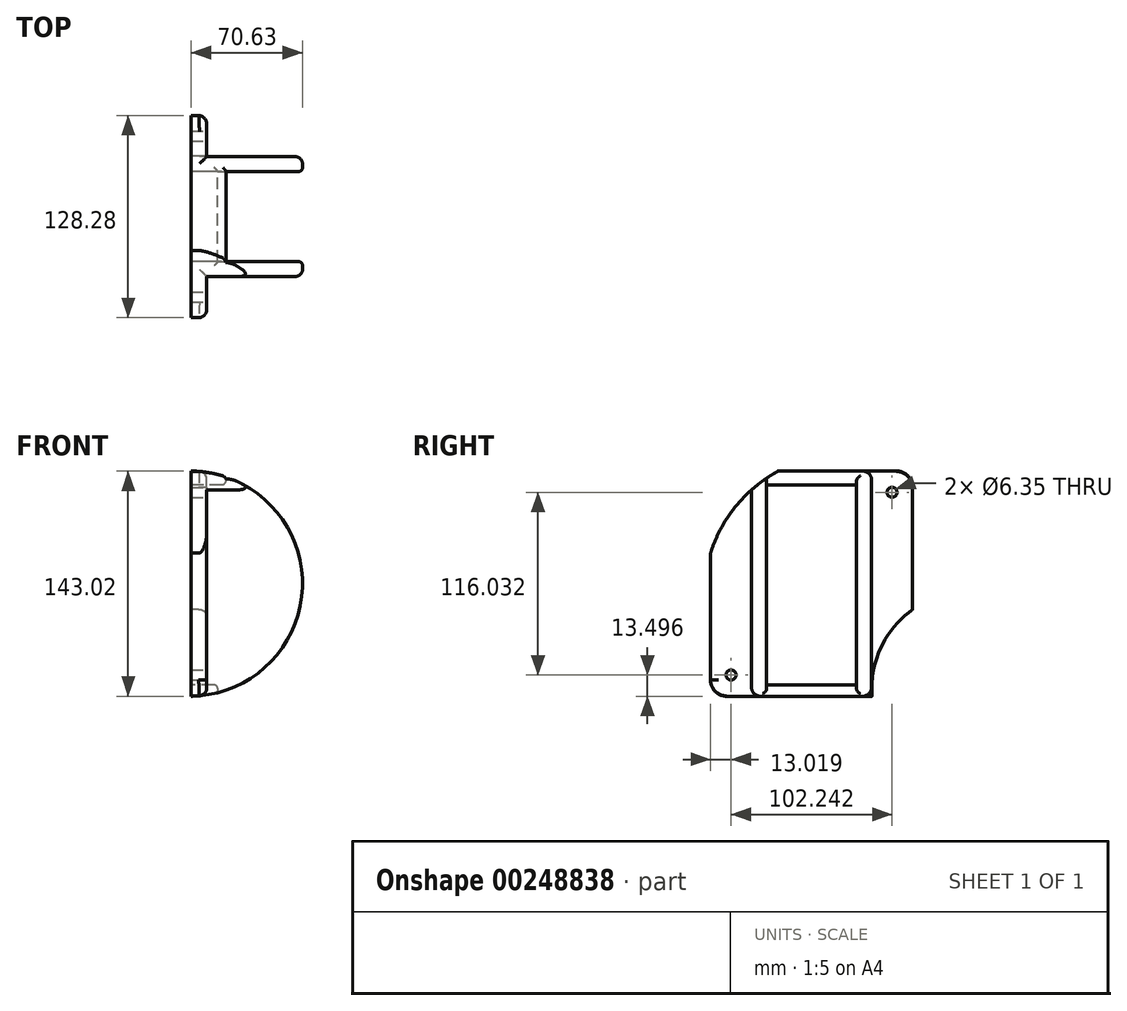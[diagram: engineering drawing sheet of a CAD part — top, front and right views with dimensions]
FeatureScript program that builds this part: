
annotation { "Feature Type Name" : "Feature", "Feature Type Description" : "" }
export const myFeature = defineFeature(function(context is Context, id is Id, definition is map)
    precondition{}
    {
        {
            var Q0;
            Q0=qCreatedBy(makeId("Front.planeOp"),FACE);
            var sketch = newSketch(context, id + "F0", { "sketchPlane" : qUnion([Q0])});
            skArc(sketch, "E0", {"start": v(0, -70.82) * mm, "mid": v(70.63, 0.7) * mm, "end": v(0, 72.2) * mm});
            skLineSegment(sketch, "E1", {"start": v(0, 72.2) * mm, "end": v(0, -70.82) * mm});
            skLineSegment(sketch, "E2", {"start": v(9.79, 71.4) * mm, "end": v(9.79, -70.02) * mm});
            skSolve(sketch);
        }
        {
            var Q0;
            Q0 = qSketchRegion(id + "F0", true);
            extrude(context, id + "F1", {"entities" : qUnion([Q0]), "endBound" : BoundingType.SYMMETRIC, "depth" : 76.2 * mm});
        }
        {
            var Q0;
            Q0 = qSketchRegion(id + "F0", true);
            extrude(context, id + "F2", {"entities" : qUnion([Q0]), "operationType" : NewBodyOperationType.ADD, "depth" : 25.4 * mm});
        }
        {
            var Q0;
            {var subQ0=sQuery(id+"F0.wireOp",EDGE,"E1");Q0=makeQuery(id+"F0.imprint","IMPRINT",FACE,{"disambiguationData":[TD([[makeQuery(id+"F0.imprint","IMPRINT",EDGE,{"derivedFrom":subQ0}),1.0]])]});}
            extrude(context, id + "F3", {"entities" : qUnion([Q0]), "operationType" : NewBodyOperationType.ADD, "endBound" : BoundingType.SYMMETRIC, "depth" : 128.28 * mm});
        }
        {
            var Q0;
            {var subQ0=sQuery(id+"F0.wireOp",EDGE,"E1");Q0=makeQuery(id+"F3.boolean.opBoolean","MERGE",FACE,{"derivedFrom":[makeQuery(id+"F1.opExtrude","SWEPT_FACE",FACE,{"disambiguationData":[OSD([subQ0])]}),makeQuery(id+"F3.opExtrude","SWEPT_FACE",FACE,{"disambiguationData":[OSD([subQ0])]})]});}
            var sketch = newSketch(context, id + "F4", { "sketchPlane" : qUnion([Q0])});
            skLineSegment(sketch, "E3.bottom", {"start": v(28.58, -63.5) * mm, "end": v(-28.58, -63.5) * mm});
            skLineSegment(sketch, "E3.top", {"start": v(28.58, 63.5) * mm, "end": v(-28.57, 63.5) * mm});
            skLineSegment(sketch, "E3.left", {"start": v(28.58, -63.5) * mm, "end": v(28.58, 63.5) * mm});
            skLineSegment(sketch, "E3.right", {"start": v(-28.58, -63.5) * mm, "end": v(-28.57, 63.5) * mm});
            skPoint(sketch, "E3.middle", {"position": v(0, 0) * mm});
            skSolve(sketch);
        }
        {
            var Q0;
            Q0 = qSketchRegion(id + "F4", true);
            extrude(context, id + "F5", {"entities" : qUnion([Q0]), "operationType" : NewBodyOperationType.REMOVE, "oppositeDirection" : true, "depth" : 76.2 * mm});
        }
        {
            var Q0;
            {var subQ0=sQuery(id+"F0.wireOp",EDGE,"E2");var subQ1=sQuery(id+"F0.wireOp",EDGE,"E1");var subQ2=sQuery(id+"F0.wireOp",EDGE,"E0");Q0=makeQuery(id+"F3.boolean.opBoolean","SPLIT",FACE,{"disambiguationData":[TD([makeQuery(id+"F1.opExtrude","CAP_FACE",FACE,{"disambiguationData":[OSD([subQ2,subQ1])],"isStart":true})])],"derivedFrom":makeQuery(id+"F3.opExtrude","SWEPT_FACE",FACE,{"disambiguationData":[OSD([subQ0])]})});}
            var sketch = newSketch(context, id + "F6", { "sketchPlane" : qUnion([Q0])});
            skCircle(sketch, "E4", {"center": v(51.12, 58.7) * mm, "radius": 3.18 * mm});
            skPoint(sketch, "E4.centerSnap0", {"position": v(51.12, 71.4) * mm});
            skSolve(sketch);
        }
        {
            var Q0;
            Q0=makeQuery(id+"F6.imprint","IMPRINT",FACE,{"disambiguationData":[TD([[makeQuery(id+"F6.imprint","IMPRINT",EDGE,{"derivedFrom":sQuery(id+"F6.wireOp",EDGE,"E4")}),-1.0]])]});
            var sketch = newSketch(context, id + "F7", { "sketchPlane" : qUnion([Q0])});
            skCircle(sketch, "E5", {"center": v(51.84, -57.32) * mm, "radius": 3.17 * mm});
            skSolve(sketch);
        }
        {
            var Q0;
            {var subQ0=sQuery(id+"F0.wireOp",EDGE,"E1");var subQ1=sQuery(id+"F0.wireOp",EDGE,"E0");var subQ2=sQuery(id+"F0.wireOp",EDGE,"E2");Q0=makeQuery(id+"F3.boolean.opBoolean","SPLIT",FACE,{"disambiguationData":[TD([makeQuery(id+"F1.opExtrude","CAP_FACE",FACE,{"disambiguationData":[OSD([subQ1,subQ0])],"isStart":false})])],"derivedFrom":makeQuery(id+"F3.opExtrude","SWEPT_FACE",FACE,{"disambiguationData":[OSD([subQ2])]})});}
            var sketch = newSketch(context, id + "F8", { "sketchPlane" : qUnion([Q0])});
            skCircle(sketch, "E6", {"center": v(-51.12, 58.7) * mm, "radius": 3.17 * mm});
            skPoint(sketch, "E6.centerSnap0", {"position": v(-51.12, 71.4) * mm});
            skCircle(sketch, "E7", {"center": v(-51.12, -57.32) * mm, "radius": 3.17 * mm});
            skPoint(sketch, "E7.centerSnap0", {"position": v(-51.12, -70.02) * mm});
            skSolve(sketch);
        }
        {
            var Q0;
            Q0 = qSketchRegion(id + "F8", true);
            extrude(context, id + "F9", {"entities" : qUnion([Q0]), "operationType" : NewBodyOperationType.REMOVE, "oppositeDirection" : true, "depth" : 25.4 * mm});
        }
        {
            var Q0;
            Q0 = qSketchRegion(id + "F7", true);
            extrude(context, id + "F10", {"entities" : qUnion([Q0]), "operationType" : NewBodyOperationType.REMOVE, "oppositeDirection" : true, "depth" : 25.4 * mm});
        }
        {
            var Q0;
            Q0 = qSketchRegion(id + "F6", true);
            extrude(context, id + "F11", {"entities" : qUnion([Q0]), "operationType" : NewBodyOperationType.REMOVE, "oppositeDirection" : true, "depth" : 25.4 * mm});
        }
        {
            var Q0;
            {var subQ0=sQuery(id+"F0.wireOp",EDGE,"E0");Q0=makeQuery(id+"F3.opExtrude","CAP_EDGE",EDGE,{"disambiguationData":[OSD([subQ0]),TDD([makeQuery(id+"F0.imprint","IMPRINT",EDGE,{"disambiguationData":[TD([[makeQuery(id+"F0.imprint","INTERSECT",VERTEX,{"disambiguationData":[OD(1.0)],"derivedFrom":[subQ0,sQuery(id+"F0.wireOp",EDGE,"E1")]}),1.0]])],"derivedFrom":subQ0})])],"isStart":true});}
            var Q1;
            {var subQ0=sQuery(id+"F0.wireOp",EDGE,"E0");Q1=makeQuery(id+"F3.opExtrude","CAP_EDGE",EDGE,{"disambiguationData":[OSD([subQ0]),TDD([makeQuery(id+"F0.imprint","IMPRINT",EDGE,{"disambiguationData":[TD([[makeQuery(id+"F0.imprint","INTERSECT",VERTEX,{"disambiguationData":[OD(0.0)],"derivedFrom":[subQ0,sQuery(id+"F0.wireOp",EDGE,"E1")]}),-1.0]])],"derivedFrom":subQ0})])],"isStart":true});}
            var Q2;
            {var subQ0=sQuery(id+"F0.wireOp",EDGE,"E0");Q2=makeQuery(id+"F3.opExtrude","CAP_EDGE",EDGE,{"disambiguationData":[OSD([subQ0]),TDD([makeQuery(id+"F0.imprint","IMPRINT",EDGE,{"disambiguationData":[TD([[makeQuery(id+"F0.imprint","INTERSECT",VERTEX,{"disambiguationData":[OD(0.0)],"derivedFrom":[subQ0,sQuery(id+"F0.wireOp",EDGE,"E1")]}),-1.0]])],"derivedFrom":subQ0})])],"isStart":false});}
            var Q3;
            {var subQ0=sQuery(id+"F0.wireOp",EDGE,"E0");Q3=makeQuery(id+"F3.opExtrude","CAP_EDGE",EDGE,{"disambiguationData":[OSD([subQ0]),TDD([makeQuery(id+"F0.imprint","IMPRINT",EDGE,{"disambiguationData":[TD([[makeQuery(id+"F0.imprint","INTERSECT",VERTEX,{"disambiguationData":[OD(1.0)],"derivedFrom":[subQ0,sQuery(id+"F0.wireOp",EDGE,"E1")]}),1.0]])],"derivedFrom":subQ0})])],"isStart":false});}
            fillet(context, id + "F12", {"entities" : qUnion([Q0, Q1, Q2, Q3]), "radius" : 10.16 * mm, "tangentPropagation" : true, "allowEdgeOverflow" : false});
        }
        {
            var Q0;
            {var subQ0=sQuery(id+"F0.wireOp",EDGE,"E1");var subQ1=sQuery(id+"F0.wireOp",EDGE,"E0");Q0=makeQuery(id+"F5.boolean.opBoolean","INTERSECT",EDGE,{"derivedFrom":[makeQuery(id+"F3.boolean.opBoolean","MERGE",FACE,{"derivedFrom":[makeQuery(id+"F1.opExtrude","SWEPT_FACE",FACE,{"disambiguationData":[OSD([subQ1])]}),makeQuery(id+"F3.opExtrude","SWEPT_FACE",FACE,{"disambiguationData":[OSD([subQ1]),TDD([makeQuery(id+"F0.imprint","IMPRINT",EDGE,{"disambiguationData":[TD([[makeQuery(id+"F0.imprint","INTERSECT",VERTEX,{"disambiguationData":[OD(0.0)],"derivedFrom":[subQ1,subQ0]}),-1.0]])],"derivedFrom":subQ1})])]}),makeQuery(id+"F3.opExtrude","SWEPT_FACE",FACE,{"disambiguationData":[OSD([subQ1]),TDD([makeQuery(id+"F0.imprint","IMPRINT",EDGE,{"disambiguationData":[TD([[makeQuery(id+"F0.imprint","INTERSECT",VERTEX,{"disambiguationData":[OD(1.0)],"derivedFrom":[subQ1,subQ0]}),1.0]])],"derivedFrom":subQ1})])]})]}),makeQuery(id+"F5.opExtrude","SWEPT_FACE",FACE,{"disambiguationData":[OSD([sQuery(id+"F4.wireOp",EDGE,"E3.bottom")])]})]});}
            var Q1;
            {var subQ0=sQuery(id+"F0.wireOp",EDGE,"E1");var subQ1=sQuery(id+"F0.wireOp",EDGE,"E0");Q1=makeQuery(id+"F5.boolean.opBoolean","INTERSECT",EDGE,{"derivedFrom":[makeQuery(id+"F3.boolean.opBoolean","MERGE",FACE,{"derivedFrom":[makeQuery(id+"F1.opExtrude","SWEPT_FACE",FACE,{"disambiguationData":[OSD([subQ1])]}),makeQuery(id+"F3.opExtrude","SWEPT_FACE",FACE,{"disambiguationData":[OSD([subQ1]),TDD([makeQuery(id+"F0.imprint","IMPRINT",EDGE,{"disambiguationData":[TD([[makeQuery(id+"F0.imprint","INTERSECT",VERTEX,{"disambiguationData":[OD(0.0)],"derivedFrom":[subQ1,subQ0]}),-1.0]])],"derivedFrom":subQ1})])]}),makeQuery(id+"F3.opExtrude","SWEPT_FACE",FACE,{"disambiguationData":[OSD([subQ1]),TDD([makeQuery(id+"F0.imprint","IMPRINT",EDGE,{"disambiguationData":[TD([[makeQuery(id+"F0.imprint","INTERSECT",VERTEX,{"disambiguationData":[OD(1.0)],"derivedFrom":[subQ1,subQ0]}),1.0]])],"derivedFrom":subQ1})])]})]}),makeQuery(id+"F5.opExtrude","SWEPT_FACE",FACE,{"disambiguationData":[OSD([sQuery(id+"F4.wireOp",EDGE,"E3.top")])]})]});}
            fillet(context, id + "F13", {"entities" : qUnion([Q0, Q1]), "radius" : 2.84 * mm, "tangentPropagation" : true, "allowEdgeOverflow" : false});
        }
        {
            var Q0;
            Q0=makeQuery(id+"F1.opExtrude","CAP_EDGE",EDGE,{"disambiguationData":[OSD([sQuery(id+"F0.wireOp",EDGE,"E0")])],"isStart":true});
            var Q1;
            Q1=makeQuery(id+"F1.opExtrude","CAP_EDGE",EDGE,{"disambiguationData":[OSD([sQuery(id+"F0.wireOp",EDGE,"E0")])],"isStart":false});
            fillet(context, id + "F14", {"entities" : qUnion([Q0, Q1]), "radius" : 4.57 * mm, "tangentPropagation" : true, "allowEdgeOverflow" : false});
        }
        {
            var Q0;
            {var subQ0=sQuery(id+"F0.wireOp",EDGE,"E1");var subQ1=sQuery(id+"F0.wireOp",EDGE,"E0");Q0=makeQuery(id+"F5.boolean.opBoolean","INTERSECT",EDGE,{"derivedFrom":[makeQuery(id+"F3.boolean.opBoolean","MERGE",FACE,{"derivedFrom":[makeQuery(id+"F1.opExtrude","SWEPT_FACE",FACE,{"disambiguationData":[OSD([subQ1])]}),makeQuery(id+"F3.opExtrude","SWEPT_FACE",FACE,{"disambiguationData":[OSD([subQ1]),TDD([makeQuery(id+"F0.imprint","IMPRINT",EDGE,{"disambiguationData":[TD([[makeQuery(id+"F0.imprint","INTERSECT",VERTEX,{"disambiguationData":[OD(0.0)],"derivedFrom":[subQ1,subQ0]}),-1.0]])],"derivedFrom":subQ1})])]}),makeQuery(id+"F3.opExtrude","SWEPT_FACE",FACE,{"disambiguationData":[OSD([subQ1]),TDD([makeQuery(id+"F0.imprint","IMPRINT",EDGE,{"disambiguationData":[TD([[makeQuery(id+"F0.imprint","INTERSECT",VERTEX,{"disambiguationData":[OD(1.0)],"derivedFrom":[subQ1,subQ0]}),1.0]])],"derivedFrom":subQ1})])]})]}),makeQuery(id+"F5.opExtrude","SWEPT_FACE",FACE,{"disambiguationData":[OSD([sQuery(id+"F4.wireOp",EDGE,"E3.right")])]})]});}
            var Q1;
            {var subQ0=sQuery(id+"F0.wireOp",EDGE,"E1");var subQ1=sQuery(id+"F0.wireOp",EDGE,"E0");Q1=makeQuery(id+"F5.boolean.opBoolean","INTERSECT",EDGE,{"derivedFrom":[makeQuery(id+"F3.boolean.opBoolean","MERGE",FACE,{"derivedFrom":[makeQuery(id+"F1.opExtrude","SWEPT_FACE",FACE,{"disambiguationData":[OSD([subQ1])]}),makeQuery(id+"F3.opExtrude","SWEPT_FACE",FACE,{"disambiguationData":[OSD([subQ1]),TDD([makeQuery(id+"F0.imprint","IMPRINT",EDGE,{"disambiguationData":[TD([[makeQuery(id+"F0.imprint","INTERSECT",VERTEX,{"disambiguationData":[OD(0.0)],"derivedFrom":[subQ1,subQ0]}),-1.0]])],"derivedFrom":subQ1})])]}),makeQuery(id+"F3.opExtrude","SWEPT_FACE",FACE,{"disambiguationData":[OSD([subQ1]),TDD([makeQuery(id+"F0.imprint","IMPRINT",EDGE,{"disambiguationData":[TD([[makeQuery(id+"F0.imprint","INTERSECT",VERTEX,{"disambiguationData":[OD(1.0)],"derivedFrom":[subQ1,subQ0]}),1.0]])],"derivedFrom":subQ1})])]})]}),makeQuery(id+"F5.opExtrude","SWEPT_FACE",FACE,{"disambiguationData":[OSD([sQuery(id+"F4.wireOp",EDGE,"E3.left")])]})]});}
            fillet(context, id + "F15", {"entities" : qUnion([Q0, Q1]), "radius" : 2.54 * mm, "tangentPropagation" : true, "allowEdgeOverflow" : false});
        }
        {
            var Q0;
            Q0=makeQuery(id+"F3.opExtrude","CAP_EDGE",EDGE,{"disambiguationData":[OSD([sQuery(id+"F0.wireOp",EDGE,"E2")])],"isStart":true});
            var Q1;
            Q1=makeQuery(id+"F3.opExtrude","CAP_EDGE",EDGE,{"disambiguationData":[OSD([sQuery(id+"F0.wireOp",EDGE,"E2")])],"isStart":false});
            fillet(context, id + "F16", {"entities" : qUnion([Q0, Q1]), "radius" : 5.08 * mm, "tangentPropagation" : true, "allowEdgeOverflow" : false});
        }
        {
            var Q0;
            Q0=qCreatedBy(makeId("Right.planeOp"),FACE);
            var sketch = newSketch(context, id + "F17", { "sketchPlane" : qUnion([Q0])});
            skArc(sketch, "E8", {"start": v(-21.5, 71.99) * mm, "mid": v(-48.07, 49.85) * mm, "end": v(-64.38, 19.34) * mm});
            skArc(sketch, "E9", {"start": v(-21.5, 71.99) * mm, "mid": v(-74.45, 71.33) * mm, "end": v(-64.38, 19.34) * mm});
            skSolve(sketch);
        }
        {
            var Q0;
            Q0 = qSketchRegion(id + "F17", true);
            extrude(context, id + "F18", {"entities" : qUnion([Q0]), "operationType" : NewBodyOperationType.REMOVE, "endBound" : BoundingType.SYMMETRIC, "oppositeDirection" : true, "depth" : 76.2 * mm});
        }
        {
            var Q0;
            Q0=qCreatedBy(makeId("Right.planeOp"),FACE);
            var sketch = newSketch(context, id + "F19", { "sketchPlane" : qUnion([Q0])});
            skCircle(sketch, "E10", {"center": v(99.59, -65.87) * mm, "radius": 61.3 * mm});
            skSolve(sketch);
        }
        {
            var Q0;
            Q0=makeQuery(id+"F19.imprint","IMPRINT",FACE,{"disambiguationData":[TD([[makeQuery(id+"F19.imprint","IMPRINT",EDGE,{"derivedFrom":sQuery(id+"F19.wireOp",EDGE,"E10")}),1.0]])]});
            extrude(context, id + "F20", {"entities" : qUnion([Q0]), "operationType" : NewBodyOperationType.REMOVE, "endBound" : BoundingType.SYMMETRIC, "depth" : 101.6 * mm});
        }
    });
